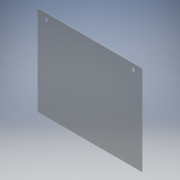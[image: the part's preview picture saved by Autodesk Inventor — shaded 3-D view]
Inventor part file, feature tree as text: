
AUTODESK INVENTOR PART (.ipt)
format: ipt  version: 2017 (Build 210142000, 142)  size: 108,032 bytes
history: native  units: in
note: dims shown in document units (in); Inventor stores cm internally (conversion verified against a paired STEP export)
features: extrude x1, sketch x1
ambient origin geometry x8: Origin, YZ Plane, XZ Plane, XY Plane, X Axis, Y Axis, Z Axis, Center Point
bodies: Body1 (feature_tree)
feature tree (2):
  extrude  "Extrusion2"  Depth=31.0in
  sketch  "Sketch1"  dims[d0=36.0in d1=31.0in d2=1.0in d5=2.0in d7=3.0in d11=0.5in d12=1.5in d13=0.093in d14=0.0in d17=1.5in d18=3.0in d19=2.0in d20=0.5in d21=1.0001in]
